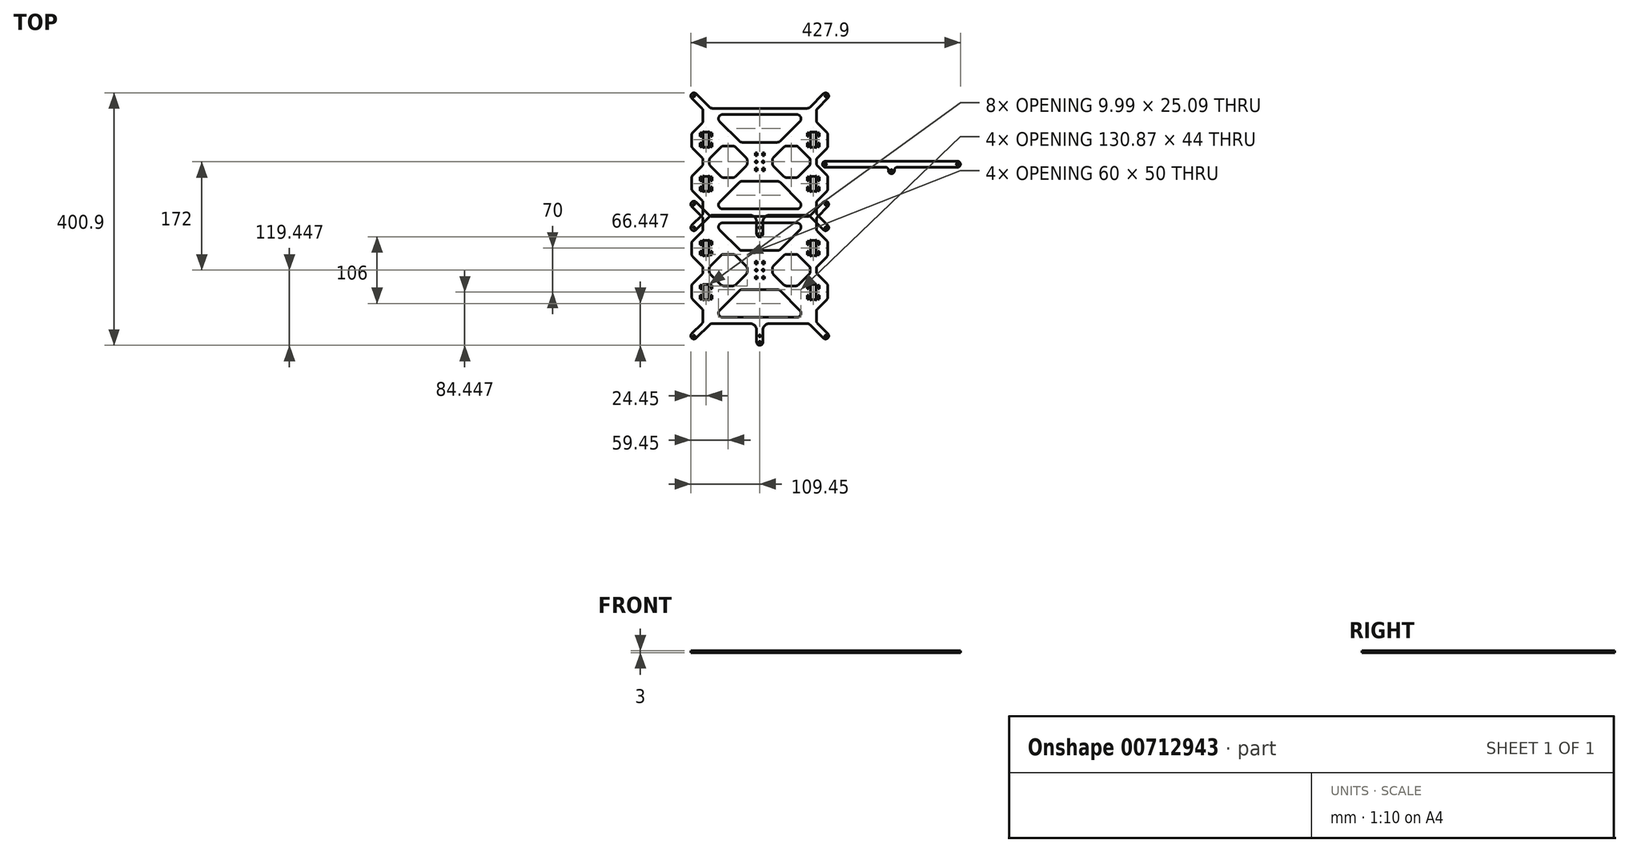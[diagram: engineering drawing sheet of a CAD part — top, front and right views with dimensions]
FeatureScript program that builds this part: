
annotation { "Feature Type Name" : "Feature", "Feature Type Description" : "" }
export const myFeature = defineFeature(function(context is Context, id is Id, definition is map)
    precondition{}
    {
        {
            var Q0;
            Q0=qCreatedBy(makeId("Top.planeOp"),FACE);
            var sketch = newSketch(context, id + "F0", { "sketchPlane" : qUnion([Q0])});
            skCircle(sketch, "E0", {"center": v(5.5, 8.85) * mm, "radius": 1.6 * mm});
            skCircle(sketch, "E1", {"center": v(-104.5, -95.65) * mm, "radius": 1.25 * mm});
            skCircle(sketch, "E2", {"center": v(-104.5, 113.35) * mm, "radius": 1.25 * mm});
            skCircle(sketch, "E3", {"center": v(0, -105.65) * mm, "radius": 1.6 * mm});
            skArc(sketch, "E4", {"start": v(-91.76, 70.09) * mm, "mid": v(-90.46, 72.04) * mm, "end": v(-90, 74.33) * mm});
            skLineSegment(sketch, "E5", {"start": v(-91.76, 70.09) * mm, "end": v(-106.24, 55.6) * mm});
            skArc(sketch, "E6", {"start": v(-106.24, 55.6) * mm, "mid": v(-107.54, 53.66) * mm, "end": v(-108, 51.36) * mm});
            skLineSegment(sketch, "E7", {"start": v(-108, 51.36) * mm, "end": v(-108, 34.33) * mm});
            skArc(sketch, "E8", {"start": v(-108, 34.33) * mm, "mid": v(-107.54, 32.04) * mm, "end": v(-106.24, 30.09) * mm});
            skLineSegment(sketch, "E9", {"start": v(-106.24, 30.09) * mm, "end": v(-91.76, 15.6) * mm});
            skArc(sketch, "E10", {"start": v(-90, 11.36) * mm, "mid": v(-90.46, 13.66) * mm, "end": v(-91.76, 15.6) * mm});
            skLineSegment(sketch, "E11", {"start": v(-90, 11.36) * mm, "end": v(-90, 6.33) * mm});
            skArc(sketch, "E12", {"start": v(-91.76, 2.09) * mm, "mid": v(-90.46, 4.04) * mm, "end": v(-90, 6.33) * mm});
            skLineSegment(sketch, "E13", {"start": v(-91.76, 2.09) * mm, "end": v(-106.24, -12.4) * mm});
            skArc(sketch, "E14", {"start": v(-106.24, -12.4) * mm, "mid": v(-107.54, -14.34) * mm, "end": v(-108, -16.64) * mm});
            skLineSegment(sketch, "E15", {"start": v(-108, -16.64) * mm, "end": v(-108, -33.67) * mm});
            skArc(sketch, "E16", {"start": v(-108, -33.67) * mm, "mid": v(-107.54, -35.96) * mm, "end": v(-106.24, -37.91) * mm});
            skLineSegment(sketch, "E17", {"start": v(-106.24, -37.91) * mm, "end": v(-91.76, -52.4) * mm});
            skArc(sketch, "E18", {"start": v(-90, -56.64) * mm, "mid": v(-90.46, -54.34) * mm, "end": v(-91.76, -52.4) * mm});
            skLineSegment(sketch, "E19", {"start": v(-90, -56.64) * mm, "end": v(-90, -71.67) * mm});
            skArc(sketch, "E20", {"start": v(-91.76, -75.91) * mm, "mid": v(-90.46, -73.96) * mm, "end": v(-90, -71.67) * mm});
            skLineSegment(sketch, "E21", {"start": v(-91.76, -75.91) * mm, "end": v(-108, -92.15) * mm});
            skArc(sketch, "E22", {"start": v(-108, -92.15) * mm, "mid": v(-108, -99.15) * mm, "end": v(-101, -99.15) * mm});
            skLineSegment(sketch, "E23", {"start": v(-101, -99.15) * mm, "end": v(-79.76, -77.91) * mm});
            skArc(sketch, "E24", {"start": v(-75.51, -76.15) * mm, "mid": v(-77.81, -76.6) * mm, "end": v(-79.76, -77.91) * mm});
            skLineSegment(sketch, "E25", {"start": v(-75.51, -76.15) * mm, "end": v(-14.95, -76.15) * mm});
            skArc(sketch, "E26", {"start": v(-4.95, -86.15) * mm, "mid": v(-7.88, -79.08) * mm, "end": v(-14.95, -76.15) * mm});
            skLineSegment(sketch, "E27", {"start": v(-4.95, -86.15) * mm, "end": v(-4.95, -105.65) * mm});
            skArc(sketch, "E28", {"start": v(-4.95, -105.65) * mm, "mid": v(0, -110.6) * mm, "end": v(4.95, -105.65) * mm});
            skLineSegment(sketch, "E29", {"start": v(4.95, -105.65) * mm, "end": v(4.95, -86.15) * mm});
            skArc(sketch, "E30", {"start": v(14.95, -76.15) * mm, "mid": v(7.88, -79.08) * mm, "end": v(4.95, -86.15) * mm});
            skLineSegment(sketch, "E31", {"start": v(14.95, -76.15) * mm, "end": v(75.51, -76.15) * mm});
            skArc(sketch, "E32", {"start": v(79.76, -77.91) * mm, "mid": v(77.81, -76.6) * mm, "end": v(75.51, -76.15) * mm});
            skLineSegment(sketch, "E33", {"start": v(79.76, -77.91) * mm, "end": v(101, -99.15) * mm});
            skArc(sketch, "E34", {"start": v(101, -99.15) * mm, "mid": v(108, -99.15) * mm, "end": v(108, -92.15) * mm});
            skLineSegment(sketch, "E35", {"start": v(108, -92.15) * mm, "end": v(91.76, -75.91) * mm});
            skArc(sketch, "E36", {"start": v(90, -71.67) * mm, "mid": v(90.46, -73.96) * mm, "end": v(91.76, -75.91) * mm});
            skLineSegment(sketch, "E37", {"start": v(90, -71.67) * mm, "end": v(90, -56.64) * mm});
            skArc(sketch, "E38", {"start": v(91.76, -52.4) * mm, "mid": v(90.46, -54.34) * mm, "end": v(90, -56.64) * mm});
            skLineSegment(sketch, "E39", {"start": v(91.76, -52.4) * mm, "end": v(106.24, -37.91) * mm});
            skArc(sketch, "E40", {"start": v(106.24, -37.91) * mm, "mid": v(107.54, -35.96) * mm, "end": v(108, -33.67) * mm});
            skLineSegment(sketch, "E41", {"start": v(108, -33.67) * mm, "end": v(108, -16.64) * mm});
            skArc(sketch, "E42", {"start": v(108, -16.64) * mm, "mid": v(107.54, -14.34) * mm, "end": v(106.24, -12.4) * mm});
            skLineSegment(sketch, "E43", {"start": v(106.24, -12.4) * mm, "end": v(91.76, 2.09) * mm});
            skArc(sketch, "E44", {"start": v(90, 6.33) * mm, "mid": v(90.46, 4.04) * mm, "end": v(91.76, 2.09) * mm});
            skLineSegment(sketch, "E45", {"start": v(90, 6.33) * mm, "end": v(90, 11.36) * mm});
            skArc(sketch, "E46", {"start": v(91.76, 15.6) * mm, "mid": v(90.46, 13.66) * mm, "end": v(90, 11.36) * mm});
            skLineSegment(sketch, "E47", {"start": v(91.76, 15.6) * mm, "end": v(106.24, 30.09) * mm});
            skArc(sketch, "E48", {"start": v(106.24, 30.09) * mm, "mid": v(107.54, 32.04) * mm, "end": v(108, 34.33) * mm});
            skLineSegment(sketch, "E49", {"start": v(108, 34.33) * mm, "end": v(108, 51.36) * mm});
            skArc(sketch, "E50", {"start": v(108, 51.36) * mm, "mid": v(107.54, 53.66) * mm, "end": v(106.24, 55.6) * mm});
            skLineSegment(sketch, "E51", {"start": v(106.24, 55.6) * mm, "end": v(91.76, 70.09) * mm});
            skArc(sketch, "E52", {"start": v(90, 74.33) * mm, "mid": v(90.46, 72.04) * mm, "end": v(91.76, 70.09) * mm});
            skLineSegment(sketch, "E53", {"start": v(90, 74.33) * mm, "end": v(90, 89.36) * mm});
            skArc(sketch, "E54", {"start": v(91.76, 93.6) * mm, "mid": v(90.46, 91.66) * mm, "end": v(90, 89.36) * mm});
            skLineSegment(sketch, "E55", {"start": v(91.76, 93.6) * mm, "end": v(108, 109.85) * mm});
            skArc(sketch, "E56", {"start": v(108, 109.85) * mm, "mid": v(108, 116.85) * mm, "end": v(101, 116.85) * mm});
            skLineSegment(sketch, "E57", {"start": v(101, 116.85) * mm, "end": v(79.76, 95.6) * mm});
            skArc(sketch, "E58", {"start": v(75.51, 93.85) * mm, "mid": v(77.81, 94.3) * mm, "end": v(79.76, 95.6) * mm});
            skLineSegment(sketch, "E59", {"start": v(75.51, 93.85) * mm, "end": v(-75.51, 93.85) * mm});
            skArc(sketch, "E60", {"start": v(-79.76, 95.6) * mm, "mid": v(-77.81, 94.3) * mm, "end": v(-75.51, 93.85) * mm});
            skLineSegment(sketch, "E61", {"start": v(-79.76, 95.6) * mm, "end": v(-101, 116.85) * mm});
            skArc(sketch, "E62", {"start": v(-101, 116.85) * mm, "mid": v(-108, 116.85) * mm, "end": v(-108, 109.85) * mm});
            skLineSegment(sketch, "E63", {"start": v(-108, 109.85) * mm, "end": v(-91.76, 93.6) * mm});
            skArc(sketch, "E64", {"start": v(-90, 89.36) * mm, "mid": v(-90.46, 91.66) * mm, "end": v(-91.76, 93.6) * mm});
            skLineSegment(sketch, "E65", {"start": v(-90, 89.36) * mm, "end": v(-90, 74.33) * mm});
            skLineSegment(sketch, "E66", {"start": v(89.5, -37.34) * mm, "end": v(89.5, -14.97) * mm});
            skArc(sketch, "E67", {"start": v(89.5, -37.34) * mm, "mid": v(89.57, -37.59) * mm, "end": v(89.75, -37.77) * mm});
            skArc(sketch, "E68", {"start": v(89.07, -38.45) * mm, "mid": v(89.85, -38.56) * mm, "end": v(89.75, -37.77) * mm});
            skArc(sketch, "E69", {"start": v(89.07, -38.45) * mm, "mid": v(88.88, -38.27) * mm, "end": v(88.63, -38.2) * mm});
            skLineSegment(sketch, "E70", {"start": v(81.37, -38.2) * mm, "end": v(88.63, -38.2) * mm});
            skArc(sketch, "E71", {"start": v(81.37, -38.2) * mm, "mid": v(81.12, -38.27) * mm, "end": v(80.93, -38.45) * mm});
            skArc(sketch, "E72", {"start": v(80.25, -37.77) * mm, "mid": v(80.15, -38.56) * mm, "end": v(80.93, -38.45) * mm});
            skArc(sketch, "E73", {"start": v(80.25, -37.77) * mm, "mid": v(80.43, -37.59) * mm, "end": v(80.5, -37.34) * mm});
            skLineSegment(sketch, "E74", {"start": v(80.5, -14.97) * mm, "end": v(80.5, -37.34) * mm});
            skArc(sketch, "E75", {"start": v(80.5, -14.97) * mm, "mid": v(80.43, -14.72) * mm, "end": v(80.25, -14.54) * mm});
            skArc(sketch, "E76", {"start": v(80.93, -13.85) * mm, "mid": v(80.15, -13.75) * mm, "end": v(80.25, -14.54) * mm});
            skArc(sketch, "E77", {"start": v(80.93, -13.85) * mm, "mid": v(81.12, -14.04) * mm, "end": v(81.37, -14.1) * mm});
            skLineSegment(sketch, "E78", {"start": v(88.63, -14.1) * mm, "end": v(81.37, -14.1) * mm});
            skArc(sketch, "E79", {"start": v(88.63, -14.1) * mm, "mid": v(88.88, -14.04) * mm, "end": v(89.07, -13.85) * mm});
            skArc(sketch, "E80", {"start": v(89.75, -14.54) * mm, "mid": v(89.85, -13.75) * mm, "end": v(89.07, -13.85) * mm});
            skArc(sketch, "E81", {"start": v(89.75, -14.54) * mm, "mid": v(89.57, -14.72) * mm, "end": v(89.5, -14.97) * mm});
            skLineSegment(sketch, "E82", {"start": v(32.73, 41.78) * mm, "end": v(63.53, 72.58) * mm});
            skArc(sketch, "E83", {"start": v(28.07, 39.85) * mm, "mid": v(30.6, 40.35) * mm, "end": v(32.73, 41.78) * mm});
            skLineSegment(sketch, "E84", {"start": v(-28.07, 39.85) * mm, "end": v(28.07, 39.85) * mm});
            skArc(sketch, "E85", {"start": v(-32.73, 41.78) * mm, "mid": v(-30.6, 40.35) * mm, "end": v(-28.07, 39.85) * mm});
            skLineSegment(sketch, "E86", {"start": v(-63.53, 72.58) * mm, "end": v(-32.73, 41.78) * mm});
            skArc(sketch, "E87", {"start": v(-58.87, 83.85) * mm, "mid": v(-64.96, 79.77) * mm, "end": v(-63.53, 72.58) * mm});
            skLineSegment(sketch, "E88", {"start": v(58.87, 83.85) * mm, "end": v(-58.87, 83.85) * mm});
            skArc(sketch, "E89", {"start": v(63.53, 72.58) * mm, "mid": v(64.96, 79.77) * mm, "end": v(58.87, 83.85) * mm});
            skLineSegment(sketch, "E90", {"start": v(21.76, 2.09) * mm, "end": v(38.24, -14.4) * mm});
            skArc(sketch, "E91", {"start": v(20, 6.33) * mm, "mid": v(20.46, 4.04) * mm, "end": v(21.76, 2.09) * mm});
            skLineSegment(sketch, "E92", {"start": v(20, 11.36) * mm, "end": v(20, 6.33) * mm});
            skArc(sketch, "E93", {"start": v(21.76, 15.6) * mm, "mid": v(20.46, 13.66) * mm, "end": v(20, 11.36) * mm});
            skLineSegment(sketch, "E94", {"start": v(38.24, 32.09) * mm, "end": v(21.76, 15.6) * mm});
            skArc(sketch, "E95", {"start": v(42.49, 33.85) * mm, "mid": v(40.19, 33.4) * mm, "end": v(38.24, 32.09) * mm});
            skLineSegment(sketch, "E96", {"start": v(57.51, 33.85) * mm, "end": v(42.49, 33.85) * mm});
            skArc(sketch, "E97", {"start": v(61.76, 32.09) * mm, "mid": v(59.81, 33.4) * mm, "end": v(57.51, 33.85) * mm});
            skLineSegment(sketch, "E98", {"start": v(78.24, 15.6) * mm, "end": v(61.76, 32.09) * mm});
            skArc(sketch, "E99", {"start": v(80, 11.36) * mm, "mid": v(79.54, 13.66) * mm, "end": v(78.24, 15.6) * mm});
            skLineSegment(sketch, "E100", {"start": v(80, 6.33) * mm, "end": v(80, 11.36) * mm});
            skArc(sketch, "E101", {"start": v(78.24, 2.09) * mm, "mid": v(79.54, 4.04) * mm, "end": v(80, 6.33) * mm});
            skLineSegment(sketch, "E102", {"start": v(61.76, -14.4) * mm, "end": v(78.24, 2.09) * mm});
            skArc(sketch, "E103", {"start": v(57.51, -16.15) * mm, "mid": v(59.81, -15.7) * mm, "end": v(61.76, -14.4) * mm});
            skLineSegment(sketch, "E104", {"start": v(42.49, -16.15) * mm, "end": v(57.51, -16.15) * mm});
            skArc(sketch, "E105", {"start": v(38.24, -14.4) * mm, "mid": v(40.19, -15.7) * mm, "end": v(42.49, -16.15) * mm});
            skLineSegment(sketch, "E106", {"start": v(63.53, -54.89) * mm, "end": v(32.73, -24.09) * mm});
            skArc(sketch, "E107", {"start": v(58.87, -66.15) * mm, "mid": v(64.96, -62.08) * mm, "end": v(63.53, -54.89) * mm});
            skLineSegment(sketch, "E108", {"start": v(-58.87, -66.15) * mm, "end": v(58.87, -66.15) * mm});
            skArc(sketch, "E109", {"start": v(-63.53, -54.89) * mm, "mid": v(-64.96, -62.08) * mm, "end": v(-58.87, -66.15) * mm});
            skLineSegment(sketch, "E110", {"start": v(-32.73, -24.09) * mm, "end": v(-63.53, -54.89) * mm});
            skArc(sketch, "E111", {"start": v(-28.07, -22.15) * mm, "mid": v(-30.6, -22.66) * mm, "end": v(-32.73, -24.09) * mm});
            skLineSegment(sketch, "E112", {"start": v(28.07, -22.15) * mm, "end": v(-28.07, -22.15) * mm});
            skArc(sketch, "E113", {"start": v(32.73, -24.09) * mm, "mid": v(30.6, -22.66) * mm, "end": v(28.07, -22.15) * mm});
            skLineSegment(sketch, "E114", {"start": v(-61.76, 32.09) * mm, "end": v(-78.24, 15.6) * mm});
            skArc(sketch, "E115", {"start": v(-57.51, 33.85) * mm, "mid": v(-59.81, 33.4) * mm, "end": v(-61.76, 32.09) * mm});
            skLineSegment(sketch, "E116", {"start": v(-42.49, 33.85) * mm, "end": v(-57.51, 33.85) * mm});
            skArc(sketch, "E117", {"start": v(-38.24, 32.09) * mm, "mid": v(-40.19, 33.4) * mm, "end": v(-42.49, 33.85) * mm});
            skLineSegment(sketch, "E118", {"start": v(-21.76, 15.6) * mm, "end": v(-38.24, 32.09) * mm});
            skArc(sketch, "E119", {"start": v(-20, 11.36) * mm, "mid": v(-20.46, 13.66) * mm, "end": v(-21.76, 15.6) * mm});
            skLineSegment(sketch, "E120", {"start": v(-20, 6.33) * mm, "end": v(-20, 11.36) * mm});
            skArc(sketch, "E121", {"start": v(-21.76, 2.09) * mm, "mid": v(-20.46, 4.04) * mm, "end": v(-20, 6.33) * mm});
            skLineSegment(sketch, "E122", {"start": v(-38.24, -14.4) * mm, "end": v(-21.76, 2.09) * mm});
            skArc(sketch, "E123", {"start": v(-42.49, -16.15) * mm, "mid": v(-40.19, -15.7) * mm, "end": v(-38.24, -14.4) * mm});
            skLineSegment(sketch, "E124", {"start": v(-57.51, -16.15) * mm, "end": v(-42.49, -16.15) * mm});
            skArc(sketch, "E125", {"start": v(-61.76, -14.4) * mm, "mid": v(-59.81, -15.7) * mm, "end": v(-57.51, -16.15) * mm});
            skLineSegment(sketch, "E126", {"start": v(-78.24, 2.09) * mm, "end": v(-61.76, -14.4) * mm});
            skArc(sketch, "E127", {"start": v(-80, 6.33) * mm, "mid": v(-79.54, 4.04) * mm, "end": v(-78.24, 2.09) * mm});
            skLineSegment(sketch, "E128", {"start": v(-80, 11.36) * mm, "end": v(-80, 6.33) * mm});
            skArc(sketch, "E129", {"start": v(-78.24, 15.6) * mm, "mid": v(-79.54, 13.66) * mm, "end": v(-80, 11.36) * mm});
            skLineSegment(sketch, "E130", {"start": v(-88.63, 31.8) * mm, "end": v(-81.37, 31.8) * mm});
            skArc(sketch, "E131", {"start": v(-88.63, 31.8) * mm, "mid": v(-88.88, 31.73) * mm, "end": v(-89.07, 31.55) * mm});
            skArc(sketch, "E132", {"start": v(-89.75, 32.23) * mm, "mid": v(-89.85, 31.44) * mm, "end": v(-89.07, 31.55) * mm});
            skArc(sketch, "E133", {"start": v(-89.75, 32.23) * mm, "mid": v(-89.57, 32.41) * mm, "end": v(-89.5, 32.66) * mm});
            skLineSegment(sketch, "E134", {"start": v(-89.5, 55.03) * mm, "end": v(-89.5, 32.66) * mm});
            skArc(sketch, "E135", {"start": v(-89.5, 55.03) * mm, "mid": v(-89.57, 55.28) * mm, "end": v(-89.75, 55.46) * mm});
            skArc(sketch, "E136", {"start": v(-89.07, 56.15) * mm, "mid": v(-89.85, 56.25) * mm, "end": v(-89.75, 55.46) * mm});
            skArc(sketch, "E137", {"start": v(-89.07, 56.15) * mm, "mid": v(-88.88, 55.96) * mm, "end": v(-88.63, 55.9) * mm});
            skLineSegment(sketch, "E138", {"start": v(-81.37, 55.9) * mm, "end": v(-88.63, 55.9) * mm});
            skArc(sketch, "E139", {"start": v(-81.37, 55.9) * mm, "mid": v(-81.12, 55.96) * mm, "end": v(-80.93, 56.15) * mm});
            skArc(sketch, "E140", {"start": v(-80.25, 55.46) * mm, "mid": v(-80.15, 56.25) * mm, "end": v(-80.93, 56.15) * mm});
            skArc(sketch, "E141", {"start": v(-80.25, 55.46) * mm, "mid": v(-80.43, 55.28) * mm, "end": v(-80.5, 55.03) * mm});
            skLineSegment(sketch, "E142", {"start": v(-80.5, 32.66) * mm, "end": v(-80.5, 55.03) * mm});
            skArc(sketch, "E143", {"start": v(-80.5, 32.66) * mm, "mid": v(-80.43, 32.41) * mm, "end": v(-80.25, 32.23) * mm});
            skArc(sketch, "E144", {"start": v(-80.93, 31.55) * mm, "mid": v(-80.15, 31.44) * mm, "end": v(-80.25, 32.23) * mm});
            skArc(sketch, "E145", {"start": v(-80.93, 31.55) * mm, "mid": v(-81.12, 31.73) * mm, "end": v(-81.37, 31.8) * mm});
            skLineSegment(sketch, "E146", {"start": v(-88.63, -38.2) * mm, "end": v(-81.37, -38.2) * mm});
            skArc(sketch, "E147", {"start": v(-88.63, -38.2) * mm, "mid": v(-88.88, -38.27) * mm, "end": v(-89.07, -38.45) * mm});
            skArc(sketch, "E148", {"start": v(-89.75, -37.77) * mm, "mid": v(-89.85, -38.56) * mm, "end": v(-89.07, -38.45) * mm});
            skArc(sketch, "E149", {"start": v(-89.75, -37.77) * mm, "mid": v(-89.57, -37.59) * mm, "end": v(-89.5, -37.34) * mm});
            skLineSegment(sketch, "E150", {"start": v(-89.5, -14.97) * mm, "end": v(-89.5, -37.34) * mm});
            skArc(sketch, "E151", {"start": v(-89.5, -14.97) * mm, "mid": v(-89.57, -14.72) * mm, "end": v(-89.75, -14.54) * mm});
            skArc(sketch, "E152", {"start": v(-89.07, -13.85) * mm, "mid": v(-89.85, -13.75) * mm, "end": v(-89.75, -14.54) * mm});
            skArc(sketch, "E153", {"start": v(-89.07, -13.85) * mm, "mid": v(-88.88, -14.04) * mm, "end": v(-88.63, -14.1) * mm});
            skLineSegment(sketch, "E154", {"start": v(-81.37, -14.1) * mm, "end": v(-88.63, -14.1) * mm});
            skArc(sketch, "E155", {"start": v(-81.37, -14.1) * mm, "mid": v(-81.12, -14.04) * mm, "end": v(-80.93, -13.85) * mm});
            skArc(sketch, "E156", {"start": v(-80.25, -14.54) * mm, "mid": v(-80.15, -13.75) * mm, "end": v(-80.93, -13.85) * mm});
            skArc(sketch, "E157", {"start": v(-80.25, -14.54) * mm, "mid": v(-80.43, -14.72) * mm, "end": v(-80.5, -14.97) * mm});
            skLineSegment(sketch, "E158", {"start": v(-80.5, -37.34) * mm, "end": v(-80.5, -14.97) * mm});
            skArc(sketch, "E159", {"start": v(-80.5, -37.34) * mm, "mid": v(-80.43, -37.59) * mm, "end": v(-80.25, -37.77) * mm});
            skArc(sketch, "E160", {"start": v(-80.93, -38.45) * mm, "mid": v(-80.15, -38.56) * mm, "end": v(-80.25, -37.77) * mm});
            skArc(sketch, "E161", {"start": v(-80.93, -38.45) * mm, "mid": v(-81.12, -38.27) * mm, "end": v(-81.37, -38.2) * mm});
            skLineSegment(sketch, "E162", {"start": v(89.5, 32.66) * mm, "end": v(89.5, 55.03) * mm});
            skArc(sketch, "E163", {"start": v(89.5, 32.66) * mm, "mid": v(89.57, 32.41) * mm, "end": v(89.75, 32.23) * mm});
            skArc(sketch, "E164", {"start": v(89.07, 31.55) * mm, "mid": v(89.85, 31.44) * mm, "end": v(89.75, 32.23) * mm});
            skArc(sketch, "E165", {"start": v(89.07, 31.55) * mm, "mid": v(88.88, 31.73) * mm, "end": v(88.63, 31.8) * mm});
            skLineSegment(sketch, "E166", {"start": v(81.37, 31.8) * mm, "end": v(88.63, 31.8) * mm});
            skArc(sketch, "E167", {"start": v(81.37, 31.8) * mm, "mid": v(81.12, 31.73) * mm, "end": v(80.93, 31.55) * mm});
            skArc(sketch, "E168", {"start": v(80.25, 32.23) * mm, "mid": v(80.15, 31.44) * mm, "end": v(80.93, 31.55) * mm});
            skArc(sketch, "E169", {"start": v(80.25, 32.23) * mm, "mid": v(80.43, 32.41) * mm, "end": v(80.5, 32.66) * mm});
            skLineSegment(sketch, "E170", {"start": v(80.5, 55.03) * mm, "end": v(80.5, 32.66) * mm});
            skArc(sketch, "E171", {"start": v(80.5, 55.03) * mm, "mid": v(80.43, 55.28) * mm, "end": v(80.25, 55.46) * mm});
            skArc(sketch, "E172", {"start": v(80.93, 56.15) * mm, "mid": v(80.15, 56.25) * mm, "end": v(80.25, 55.46) * mm});
            skArc(sketch, "E173", {"start": v(80.93, 56.15) * mm, "mid": v(81.12, 55.96) * mm, "end": v(81.37, 55.9) * mm});
            skLineSegment(sketch, "E174", {"start": v(88.63, 55.9) * mm, "end": v(81.37, 55.9) * mm});
            skArc(sketch, "E175", {"start": v(88.63, 55.9) * mm, "mid": v(88.88, 55.96) * mm, "end": v(89.07, 56.15) * mm});
            skArc(sketch, "E176", {"start": v(89.75, 55.46) * mm, "mid": v(89.85, 56.25) * mm, "end": v(89.07, 56.15) * mm});
            skArc(sketch, "E177", {"start": v(89.75, 55.46) * mm, "mid": v(89.57, 55.28) * mm, "end": v(89.5, 55.03) * mm});
            skCircle(sketch, "E178", {"center": v(0, -95.65) * mm, "radius": 1.6 * mm});
            skCircle(sketch, "E179", {"center": v(104.5, 113.35) * mm, "radius": 1.25 * mm});
            skCircle(sketch, "E180", {"center": v(104.5, -95.65) * mm, "radius": 1.25 * mm});
            skCircle(sketch, "E181", {"center": v(-5.5, 8.85) * mm, "radius": 1.6 * mm});
            skLineSegment(sketch, "E182", {"start": v(7.2, -1.05) * mm, "end": v(4, -1.05) * mm});
            skLineSegment(sketch, "E183", {"start": v(7.2, -5.25) * mm, "end": v(7.2, -1.05) * mm});
            skLineSegment(sketch, "E184", {"start": v(4, -5.25) * mm, "end": v(7.2, -5.25) * mm});
            skLineSegment(sketch, "E185", {"start": v(4, -1.05) * mm, "end": v(4, -5.25) * mm});
            skLineSegment(sketch, "E186", {"start": v(7.2, 22.95) * mm, "end": v(4, 22.95) * mm});
            skLineSegment(sketch, "E187", {"start": v(7.2, 18.75) * mm, "end": v(7.2, 22.95) * mm});
            skLineSegment(sketch, "E188", {"start": v(4, 18.75) * mm, "end": v(7.2, 18.75) * mm});
            skLineSegment(sketch, "E189", {"start": v(4, 22.95) * mm, "end": v(4, 18.75) * mm});
            skLineSegment(sketch, "E190", {"start": v(-7.2, -5.25) * mm, "end": v(-4, -5.25) * mm});
            skLineSegment(sketch, "E191", {"start": v(-7.2, -1.05) * mm, "end": v(-7.2, -5.25) * mm});
            skLineSegment(sketch, "E192", {"start": v(-4, -1.05) * mm, "end": v(-7.2, -1.05) * mm});
            skLineSegment(sketch, "E193", {"start": v(-4, -5.25) * mm, "end": v(-4, -1.05) * mm});
            skLineSegment(sketch, "E194", {"start": v(-7.2, 18.75) * mm, "end": v(-4, 18.75) * mm});
            skLineSegment(sketch, "E195", {"start": v(-7.2, 22.95) * mm, "end": v(-7.2, 18.75) * mm});
            skLineSegment(sketch, "E196", {"start": v(-4, 22.95) * mm, "end": v(-7.2, 22.95) * mm});
            skLineSegment(sketch, "E197", {"start": v(-4, 18.75) * mm, "end": v(-4, 22.95) * mm});
            skLineSegment(sketch, "E198", {"start": v(-75.5, 38.85) * mm, "end": v(-77.5, 38.85) * mm});
            skLineSegment(sketch, "E199", {"start": v(-75.5, 32.85) * mm, "end": v(-75.5, 38.85) * mm});
            skLineSegment(sketch, "E200", {"start": v(-77.5, 32.85) * mm, "end": v(-75.5, 32.85) * mm});
            skLineSegment(sketch, "E201", {"start": v(-77.5, 38.85) * mm, "end": v(-77.5, 32.85) * mm});
            skLineSegment(sketch, "E202", {"start": v(-92.5, 38.85) * mm, "end": v(-94.5, 38.85) * mm});
            skLineSegment(sketch, "E203", {"start": v(-92.5, 32.85) * mm, "end": v(-92.5, 38.85) * mm});
            skLineSegment(sketch, "E204", {"start": v(-94.5, 32.85) * mm, "end": v(-92.5, 32.85) * mm});
            skLineSegment(sketch, "E205", {"start": v(-94.5, 38.85) * mm, "end": v(-94.5, 32.85) * mm});
            skLineSegment(sketch, "E206", {"start": v(-77.5, 48.85) * mm, "end": v(-75.5, 48.85) * mm});
            skLineSegment(sketch, "E207", {"start": v(-77.5, 54.85) * mm, "end": v(-77.5, 48.85) * mm});
            skLineSegment(sketch, "E208", {"start": v(-75.5, 54.85) * mm, "end": v(-77.5, 54.85) * mm});
            skLineSegment(sketch, "E209", {"start": v(-75.5, 48.85) * mm, "end": v(-75.5, 54.85) * mm});
            skLineSegment(sketch, "E210", {"start": v(-94.5, 48.85) * mm, "end": v(-92.5, 48.85) * mm});
            skLineSegment(sketch, "E211", {"start": v(-94.5, 54.85) * mm, "end": v(-94.5, 48.85) * mm});
            skLineSegment(sketch, "E212", {"start": v(-92.5, 54.85) * mm, "end": v(-94.5, 54.85) * mm});
            skLineSegment(sketch, "E213", {"start": v(-92.5, 48.85) * mm, "end": v(-92.5, 54.85) * mm});
            skLineSegment(sketch, "E214", {"start": v(94.5, 38.85) * mm, "end": v(92.5, 38.85) * mm});
            skLineSegment(sketch, "E215", {"start": v(94.5, 32.85) * mm, "end": v(94.5, 38.85) * mm});
            skLineSegment(sketch, "E216", {"start": v(92.5, 32.85) * mm, "end": v(94.5, 32.85) * mm});
            skLineSegment(sketch, "E217", {"start": v(92.5, 38.85) * mm, "end": v(92.5, 32.85) * mm});
            skLineSegment(sketch, "E218", {"start": v(77.5, 38.85) * mm, "end": v(75.5, 38.85) * mm});
            skLineSegment(sketch, "E219", {"start": v(77.5, 32.85) * mm, "end": v(77.5, 38.85) * mm});
            skLineSegment(sketch, "E220", {"start": v(75.5, 32.85) * mm, "end": v(77.5, 32.85) * mm});
            skLineSegment(sketch, "E221", {"start": v(75.5, 38.85) * mm, "end": v(75.5, 32.85) * mm});
            skLineSegment(sketch, "E222", {"start": v(92.5, 48.85) * mm, "end": v(94.5, 48.85) * mm});
            skLineSegment(sketch, "E223", {"start": v(92.5, 54.85) * mm, "end": v(92.5, 48.85) * mm});
            skLineSegment(sketch, "E224", {"start": v(94.5, 54.85) * mm, "end": v(92.5, 54.85) * mm});
            skLineSegment(sketch, "E225", {"start": v(94.5, 48.85) * mm, "end": v(94.5, 54.85) * mm});
            skLineSegment(sketch, "E226", {"start": v(75.5, 48.85) * mm, "end": v(77.5, 48.85) * mm});
            skLineSegment(sketch, "E227", {"start": v(75.5, 54.85) * mm, "end": v(75.5, 48.85) * mm});
            skLineSegment(sketch, "E228", {"start": v(77.5, 54.85) * mm, "end": v(75.5, 54.85) * mm});
            skLineSegment(sketch, "E229", {"start": v(77.5, 48.85) * mm, "end": v(77.5, 54.85) * mm});
            skLineSegment(sketch, "E230", {"start": v(94.5, -31.15) * mm, "end": v(92.5, -31.15) * mm});
            skLineSegment(sketch, "E231", {"start": v(94.5, -37.15) * mm, "end": v(94.5, -31.15) * mm});
            skLineSegment(sketch, "E232", {"start": v(92.5, -37.15) * mm, "end": v(94.5, -37.15) * mm});
            skLineSegment(sketch, "E233", {"start": v(92.5, -31.15) * mm, "end": v(92.5, -37.15) * mm});
            skLineSegment(sketch, "E234", {"start": v(77.5, -31.15) * mm, "end": v(75.5, -31.15) * mm});
            skLineSegment(sketch, "E235", {"start": v(77.5, -37.15) * mm, "end": v(77.5, -31.15) * mm});
            skLineSegment(sketch, "E236", {"start": v(75.5, -37.15) * mm, "end": v(77.5, -37.15) * mm});
            skLineSegment(sketch, "E237", {"start": v(75.5, -31.15) * mm, "end": v(75.5, -37.15) * mm});
            skLineSegment(sketch, "E238", {"start": v(92.5, -21.15) * mm, "end": v(94.5, -21.15) * mm});
            skLineSegment(sketch, "E239", {"start": v(92.5, -15.15) * mm, "end": v(92.5, -21.15) * mm});
            skLineSegment(sketch, "E240", {"start": v(94.5, -15.15) * mm, "end": v(92.5, -15.15) * mm});
            skLineSegment(sketch, "E241", {"start": v(94.5, -21.15) * mm, "end": v(94.5, -15.15) * mm});
            skLineSegment(sketch, "E242", {"start": v(75.5, -21.15) * mm, "end": v(77.5, -21.15) * mm});
            skLineSegment(sketch, "E243", {"start": v(75.5, -15.15) * mm, "end": v(75.5, -21.15) * mm});
            skLineSegment(sketch, "E244", {"start": v(77.5, -15.15) * mm, "end": v(75.5, -15.15) * mm});
            skLineSegment(sketch, "E245", {"start": v(77.5, -21.15) * mm, "end": v(77.5, -15.15) * mm});
            skLineSegment(sketch, "E246", {"start": v(-75.5, -31.15) * mm, "end": v(-77.5, -31.15) * mm});
            skLineSegment(sketch, "E247", {"start": v(-75.5, -37.15) * mm, "end": v(-75.5, -31.15) * mm});
            skLineSegment(sketch, "E248", {"start": v(-77.5, -37.15) * mm, "end": v(-75.5, -37.15) * mm});
            skLineSegment(sketch, "E249", {"start": v(-77.5, -31.15) * mm, "end": v(-77.5, -37.15) * mm});
            skLineSegment(sketch, "E250", {"start": v(-92.5, -31.15) * mm, "end": v(-94.5, -31.15) * mm});
            skLineSegment(sketch, "E251", {"start": v(-92.5, -37.15) * mm, "end": v(-92.5, -31.15) * mm});
            skLineSegment(sketch, "E252", {"start": v(-94.5, -37.15) * mm, "end": v(-92.5, -37.15) * mm});
            skLineSegment(sketch, "E253", {"start": v(-94.5, -31.15) * mm, "end": v(-94.5, -37.15) * mm});
            skLineSegment(sketch, "E254", {"start": v(-77.5, -21.15) * mm, "end": v(-75.5, -21.15) * mm});
            skLineSegment(sketch, "E255", {"start": v(-77.5, -15.15) * mm, "end": v(-77.5, -21.15) * mm});
            skLineSegment(sketch, "E256", {"start": v(-75.5, -15.15) * mm, "end": v(-77.5, -15.15) * mm});
            skLineSegment(sketch, "E257", {"start": v(-75.5, -21.15) * mm, "end": v(-75.5, -15.15) * mm});
            skLineSegment(sketch, "E258", {"start": v(-94.5, -21.15) * mm, "end": v(-92.5, -21.15) * mm});
            skLineSegment(sketch, "E259", {"start": v(-94.5, -15.15) * mm, "end": v(-94.5, -21.15) * mm});
            skLineSegment(sketch, "E260", {"start": v(-92.5, -15.15) * mm, "end": v(-94.5, -15.15) * mm});
            skLineSegment(sketch, "E261", {"start": v(-92.5, -21.15) * mm, "end": v(-92.5, -15.15) * mm});
            skSolve(sketch);
        }
        {
            var Q0;
            Q0 = qSketchRegion(id + "F0", true);
            extrude(context, id + "F1", {"entities" : qUnion([Q0]), "depth" : 3 * mm, "offsetDistance" : 25 * mm});
        }
        {
            var Q0;
            Q0=qCreatedBy(makeId("Top.planeOp"),FACE);
            var sketch = newSketch(context, id + "F2", { "sketchPlane" : qUnion([Q0])});
            skArc(sketch, "E262", {"start": v(104.5, 0.05) * mm, "mid": v(109.45, 5) * mm, "end": v(104.5, 9.95) * mm});
            skArc(sketch, "E263", {"start": v(-104.5, 9.95) * mm, "mid": v(-109.45, 5) * mm, "end": v(-104.5, 0.05) * mm});
            skCircle(sketch, "E264", {"center": v(-104.5, 5) * mm, "radius": 1.6 * mm});
            skCircle(sketch, "E265", {"center": v(104.5, 5) * mm, "radius": 1.6 * mm});
            skArc(sketch, "E266", {"start": v(-4.95, -5) * mm, "mid": v(0, -9.95) * mm, "end": v(4.95, -5) * mm});
            skCircle(sketch, "E267", {"center": v(0, -5) * mm, "radius": 1.6 * mm});
            skLineSegment(sketch, "E268", {"start": v(-8.95, 0.05) * mm, "end": v(-104.5, 0.05) * mm});
            skLineSegment(sketch, "E269", {"start": v(-4.95, -5) * mm, "end": v(-4.95, -3.95) * mm});
            skLineSegment(sketch, "E270", {"start": v(4.95, -3.95) * mm, "end": v(4.95, -5) * mm});
            skLineSegment(sketch, "E271", {"start": v(104.5, 0.05) * mm, "end": v(8.95, 0.05) * mm});
            skLineSegment(sketch, "E272", {"start": v(-104.5, 9.95) * mm, "end": v(104.5, 9.95) * mm});
            skArc(sketch, "E273", {"start": v(8.95, 0.05) * mm, "mid": v(6.12, -1.12) * mm, "end": v(4.95, -3.95) * mm});
            skArc(sketch, "E274", {"start": v(-4.95, -3.95) * mm, "mid": v(-6.12, -1.12) * mm, "end": v(-8.95, 0.05) * mm});
            skSolve(sketch);
        }
        {
            var Q0;
            Q0 = qSketchRegion(id + "F2", true);
            extrude(context, id + "F3", {"entities" : qUnion([Q0]), "depth" : 3 * mm, "offsetDistance" : 25 * mm});
        }
        {
            var Q0;
            Q0=makeQuery(id+"F3.opExtrude","SWEPT_BODY",BODY,{"disambiguationData":[OSD([sQuery(id+"F2.wireOp",EDGE,"E262"),sQuery(id+"F2.wireOp",EDGE,"E263"),sQuery(id+"F2.wireOp",EDGE,"E264"),sQuery(id+"F2.wireOp",EDGE,"E265"),sQuery(id+"F2.wireOp",EDGE,"E266"),sQuery(id+"F2.wireOp",EDGE,"E267"),sQuery(id+"F2.wireOp",EDGE,"E268"),sQuery(id+"F2.wireOp",EDGE,"E269"),sQuery(id+"F2.wireOp",EDGE,"E270"),sQuery(id+"F2.wireOp",EDGE,"E271"),sQuery(id+"F2.wireOp",EDGE,"E272"),sQuery(id+"F2.wireOp",EDGE,"E273"),sQuery(id+"F2.wireOp",EDGE,"E274")])]});
            var Q1;
            Q1=makeQuery(id+"F3.opExtrude","CAP_EDGE",EDGE,{"disambiguationData":[OSD([sQuery(id+"F2.wireOp",EDGE,"E272")])],"isStart":false});
            transform(context, id + "F4", {"entities" : qUnion([Q0]), "transformType" : TransformType.TRANSLATION_ENTITY, "oppositeDirectionEntity" : false, "transformLine" : qUnion([Q1]), "makeCopy" : false});
        }
        {
            var Q0;
            Q0=makeQuery(id+"F1.opExtrude","SWEPT_BODY",BODY,{"disambiguationData":[OSD([sQuery(id+"F0.wireOp",EDGE,"E0"),sQuery(id+"F0.wireOp",EDGE,"E1"),sQuery(id+"F0.wireOp",EDGE,"E2"),sQuery(id+"F0.wireOp",EDGE,"E3"),sQuery(id+"F0.wireOp",EDGE,"E4"),sQuery(id+"F0.wireOp",EDGE,"E5"),sQuery(id+"F0.wireOp",EDGE,"E6"),sQuery(id+"F0.wireOp",EDGE,"E7"),sQuery(id+"F0.wireOp",EDGE,"E8"),sQuery(id+"F0.wireOp",EDGE,"E9"),sQuery(id+"F0.wireOp",EDGE,"E10"),sQuery(id+"F0.wireOp",EDGE,"E11"),sQuery(id+"F0.wireOp",EDGE,"E12"),sQuery(id+"F0.wireOp",EDGE,"E13"),sQuery(id+"F0.wireOp",EDGE,"E14"),sQuery(id+"F0.wireOp",EDGE,"E15"),sQuery(id+"F0.wireOp",EDGE,"E16"),sQuery(id+"F0.wireOp",EDGE,"E17"),sQuery(id+"F0.wireOp",EDGE,"E18"),sQuery(id+"F0.wireOp",EDGE,"E19"),sQuery(id+"F0.wireOp",EDGE,"E20"),sQuery(id+"F0.wireOp",EDGE,"E21"),sQuery(id+"F0.wireOp",EDGE,"E22"),sQuery(id+"F0.wireOp",EDGE,"E23"),sQuery(id+"F0.wireOp",EDGE,"E24"),sQuery(id+"F0.wireOp",EDGE,"E25"),sQuery(id+"F0.wireOp",EDGE,"E26"),sQuery(id+"F0.wireOp",EDGE,"E27"),sQuery(id+"F0.wireOp",EDGE,"E28"),sQuery(id+"F0.wireOp",EDGE,"E29"),sQuery(id+"F0.wireOp",EDGE,"E30"),sQuery(id+"F0.wireOp",EDGE,"E31"),sQuery(id+"F0.wireOp",EDGE,"E32"),sQuery(id+"F0.wireOp",EDGE,"E33"),sQuery(id+"F0.wireOp",EDGE,"E34"),sQuery(id+"F0.wireOp",EDGE,"E35"),sQuery(id+"F0.wireOp",EDGE,"E36"),sQuery(id+"F0.wireOp",EDGE,"E37"),sQuery(id+"F0.wireOp",EDGE,"E38"),sQuery(id+"F0.wireOp",EDGE,"E39"),sQuery(id+"F0.wireOp",EDGE,"E40"),sQuery(id+"F0.wireOp",EDGE,"E41"),sQuery(id+"F0.wireOp",EDGE,"E42"),sQuery(id+"F0.wireOp",EDGE,"E43"),sQuery(id+"F0.wireOp",EDGE,"E44"),sQuery(id+"F0.wireOp",EDGE,"E45"),sQuery(id+"F0.wireOp",EDGE,"E46"),sQuery(id+"F0.wireOp",EDGE,"E47"),sQuery(id+"F0.wireOp",EDGE,"E48"),sQuery(id+"F0.wireOp",EDGE,"E49"),sQuery(id+"F0.wireOp",EDGE,"E50"),sQuery(id+"F0.wireOp",EDGE,"E51"),sQuery(id+"F0.wireOp",EDGE,"E52"),sQuery(id+"F0.wireOp",EDGE,"E53"),sQuery(id+"F0.wireOp",EDGE,"E54"),sQuery(id+"F0.wireOp",EDGE,"E55"),sQuery(id+"F0.wireOp",EDGE,"E56"),sQuery(id+"F0.wireOp",EDGE,"E57"),sQuery(id+"F0.wireOp",EDGE,"E58"),sQuery(id+"F0.wireOp",EDGE,"E59"),sQuery(id+"F0.wireOp",EDGE,"E60"),sQuery(id+"F0.wireOp",EDGE,"E61"),sQuery(id+"F0.wireOp",EDGE,"E62"),sQuery(id+"F0.wireOp",EDGE,"E63"),sQuery(id+"F0.wireOp",EDGE,"E64"),sQuery(id+"F0.wireOp",EDGE,"E65"),sQuery(id+"F0.wireOp",EDGE,"E66"),sQuery(id+"F0.wireOp",EDGE,"E67"),sQuery(id+"F0.wireOp",EDGE,"E68"),sQuery(id+"F0.wireOp",EDGE,"E69"),sQuery(id+"F0.wireOp",EDGE,"E70"),sQuery(id+"F0.wireOp",EDGE,"E71"),sQuery(id+"F0.wireOp",EDGE,"E72"),sQuery(id+"F0.wireOp",EDGE,"E73"),sQuery(id+"F0.wireOp",EDGE,"E74"),sQuery(id+"F0.wireOp",EDGE,"E75"),sQuery(id+"F0.wireOp",EDGE,"E76"),sQuery(id+"F0.wireOp",EDGE,"E77"),sQuery(id+"F0.wireOp",EDGE,"E78"),sQuery(id+"F0.wireOp",EDGE,"E79"),sQuery(id+"F0.wireOp",EDGE,"E80"),sQuery(id+"F0.wireOp",EDGE,"E81"),sQuery(id+"F0.wireOp",EDGE,"E82"),sQuery(id+"F0.wireOp",EDGE,"E83"),sQuery(id+"F0.wireOp",EDGE,"E84"),sQuery(id+"F0.wireOp",EDGE,"E85"),sQuery(id+"F0.wireOp",EDGE,"E86"),sQuery(id+"F0.wireOp",EDGE,"E87"),sQuery(id+"F0.wireOp",EDGE,"E88"),sQuery(id+"F0.wireOp",EDGE,"E89"),sQuery(id+"F0.wireOp",EDGE,"E90"),sQuery(id+"F0.wireOp",EDGE,"E91"),sQuery(id+"F0.wireOp",EDGE,"E92"),sQuery(id+"F0.wireOp",EDGE,"E93"),sQuery(id+"F0.wireOp",EDGE,"E94"),sQuery(id+"F0.wireOp",EDGE,"E95"),sQuery(id+"F0.wireOp",EDGE,"E96"),sQuery(id+"F0.wireOp",EDGE,"E97"),sQuery(id+"F0.wireOp",EDGE,"E98"),sQuery(id+"F0.wireOp",EDGE,"E99"),sQuery(id+"F0.wireOp",EDGE,"E100"),sQuery(id+"F0.wireOp",EDGE,"E101"),sQuery(id+"F0.wireOp",EDGE,"E102"),sQuery(id+"F0.wireOp",EDGE,"E103"),sQuery(id+"F0.wireOp",EDGE,"E104"),sQuery(id+"F0.wireOp",EDGE,"E105"),sQuery(id+"F0.wireOp",EDGE,"E106"),sQuery(id+"F0.wireOp",EDGE,"E107"),sQuery(id+"F0.wireOp",EDGE,"E108"),sQuery(id+"F0.wireOp",EDGE,"E109"),sQuery(id+"F0.wireOp",EDGE,"E110"),sQuery(id+"F0.wireOp",EDGE,"E111"),sQuery(id+"F0.wireOp",EDGE,"E112"),sQuery(id+"F0.wireOp",EDGE,"E113"),sQuery(id+"F0.wireOp",EDGE,"E114"),sQuery(id+"F0.wireOp",EDGE,"E115"),sQuery(id+"F0.wireOp",EDGE,"E116"),sQuery(id+"F0.wireOp",EDGE,"E117"),sQuery(id+"F0.wireOp",EDGE,"E118"),sQuery(id+"F0.wireOp",EDGE,"E119"),sQuery(id+"F0.wireOp",EDGE,"E120"),sQuery(id+"F0.wireOp",EDGE,"E121"),sQuery(id+"F0.wireOp",EDGE,"E122"),sQuery(id+"F0.wireOp",EDGE,"E123"),sQuery(id+"F0.wireOp",EDGE,"E124"),sQuery(id+"F0.wireOp",EDGE,"E125"),sQuery(id+"F0.wireOp",EDGE,"E126"),sQuery(id+"F0.wireOp",EDGE,"E127"),sQuery(id+"F0.wireOp",EDGE,"E128"),sQuery(id+"F0.wireOp",EDGE,"E129"),sQuery(id+"F0.wireOp",EDGE,"E130"),sQuery(id+"F0.wireOp",EDGE,"E131"),sQuery(id+"F0.wireOp",EDGE,"E132"),sQuery(id+"F0.wireOp",EDGE,"E133"),sQuery(id+"F0.wireOp",EDGE,"E134"),sQuery(id+"F0.wireOp",EDGE,"E135"),sQuery(id+"F0.wireOp",EDGE,"E136"),sQuery(id+"F0.wireOp",EDGE,"E137"),sQuery(id+"F0.wireOp",EDGE,"E138"),sQuery(id+"F0.wireOp",EDGE,"E139"),sQuery(id+"F0.wireOp",EDGE,"E140"),sQuery(id+"F0.wireOp",EDGE,"E141"),sQuery(id+"F0.wireOp",EDGE,"E142"),sQuery(id+"F0.wireOp",EDGE,"E143"),sQuery(id+"F0.wireOp",EDGE,"E144"),sQuery(id+"F0.wireOp",EDGE,"E145"),sQuery(id+"F0.wireOp",EDGE,"E146"),sQuery(id+"F0.wireOp",EDGE,"E147"),sQuery(id+"F0.wireOp",EDGE,"E148"),sQuery(id+"F0.wireOp",EDGE,"E149"),sQuery(id+"F0.wireOp",EDGE,"E150"),sQuery(id+"F0.wireOp",EDGE,"E151"),sQuery(id+"F0.wireOp",EDGE,"E152"),sQuery(id+"F0.wireOp",EDGE,"E153"),sQuery(id+"F0.wireOp",EDGE,"E154"),sQuery(id+"F0.wireOp",EDGE,"E155"),sQuery(id+"F0.wireOp",EDGE,"E156"),sQuery(id+"F0.wireOp",EDGE,"E157"),sQuery(id+"F0.wireOp",EDGE,"E158"),sQuery(id+"F0.wireOp",EDGE,"E159"),sQuery(id+"F0.wireOp",EDGE,"E160"),sQuery(id+"F0.wireOp",EDGE,"E161"),sQuery(id+"F0.wireOp",EDGE,"E162"),sQuery(id+"F0.wireOp",EDGE,"E163"),sQuery(id+"F0.wireOp",EDGE,"E164"),sQuery(id+"F0.wireOp",EDGE,"E165"),sQuery(id+"F0.wireOp",EDGE,"E166"),sQuery(id+"F0.wireOp",EDGE,"E167"),sQuery(id+"F0.wireOp",EDGE,"E168"),sQuery(id+"F0.wireOp",EDGE,"E169"),sQuery(id+"F0.wireOp",EDGE,"E170"),sQuery(id+"F0.wireOp",EDGE,"E171"),sQuery(id+"F0.wireOp",EDGE,"E172"),sQuery(id+"F0.wireOp",EDGE,"E173"),sQuery(id+"F0.wireOp",EDGE,"E174"),sQuery(id+"F0.wireOp",EDGE,"E175"),sQuery(id+"F0.wireOp",EDGE,"E176"),sQuery(id+"F0.wireOp",EDGE,"E177"),sQuery(id+"F0.wireOp",EDGE,"E178"),sQuery(id+"F0.wireOp",EDGE,"E179"),sQuery(id+"F0.wireOp",EDGE,"E180"),sQuery(id+"F0.wireOp",EDGE,"E181"),sQuery(id+"F0.wireOp",EDGE,"E182"),sQuery(id+"F0.wireOp",EDGE,"E183"),sQuery(id+"F0.wireOp",EDGE,"E184"),sQuery(id+"F0.wireOp",EDGE,"E185"),sQuery(id+"F0.wireOp",EDGE,"E186"),sQuery(id+"F0.wireOp",EDGE,"E187"),sQuery(id+"F0.wireOp",EDGE,"E188"),sQuery(id+"F0.wireOp",EDGE,"E189"),sQuery(id+"F0.wireOp",EDGE,"E190"),sQuery(id+"F0.wireOp",EDGE,"E191"),sQuery(id+"F0.wireOp",EDGE,"E192"),sQuery(id+"F0.wireOp",EDGE,"E193"),sQuery(id+"F0.wireOp",EDGE,"E194"),sQuery(id+"F0.wireOp",EDGE,"E195"),sQuery(id+"F0.wireOp",EDGE,"E196"),sQuery(id+"F0.wireOp",EDGE,"E197"),sQuery(id+"F0.wireOp",EDGE,"E198"),sQuery(id+"F0.wireOp",EDGE,"E199"),sQuery(id+"F0.wireOp",EDGE,"E200"),sQuery(id+"F0.wireOp",EDGE,"E201"),sQuery(id+"F0.wireOp",EDGE,"E202"),sQuery(id+"F0.wireOp",EDGE,"E203"),sQuery(id+"F0.wireOp",EDGE,"E204"),sQuery(id+"F0.wireOp",EDGE,"E205"),sQuery(id+"F0.wireOp",EDGE,"E206"),sQuery(id+"F0.wireOp",EDGE,"E207"),sQuery(id+"F0.wireOp",EDGE,"E208"),sQuery(id+"F0.wireOp",EDGE,"E209"),sQuery(id+"F0.wireOp",EDGE,"E210"),sQuery(id+"F0.wireOp",EDGE,"E211"),sQuery(id+"F0.wireOp",EDGE,"E212"),sQuery(id+"F0.wireOp",EDGE,"E213"),sQuery(id+"F0.wireOp",EDGE,"E214"),sQuery(id+"F0.wireOp",EDGE,"E215"),sQuery(id+"F0.wireOp",EDGE,"E216"),sQuery(id+"F0.wireOp",EDGE,"E217"),sQuery(id+"F0.wireOp",EDGE,"E218"),sQuery(id+"F0.wireOp",EDGE,"E219"),sQuery(id+"F0.wireOp",EDGE,"E220"),sQuery(id+"F0.wireOp",EDGE,"E221"),sQuery(id+"F0.wireOp",EDGE,"E222"),sQuery(id+"F0.wireOp",EDGE,"E223"),sQuery(id+"F0.wireOp",EDGE,"E224"),sQuery(id+"F0.wireOp",EDGE,"E225"),sQuery(id+"F0.wireOp",EDGE,"E226"),sQuery(id+"F0.wireOp",EDGE,"E227"),sQuery(id+"F0.wireOp",EDGE,"E228"),sQuery(id+"F0.wireOp",EDGE,"E229"),sQuery(id+"F0.wireOp",EDGE,"E230"),sQuery(id+"F0.wireOp",EDGE,"E231"),sQuery(id+"F0.wireOp",EDGE,"E232"),sQuery(id+"F0.wireOp",EDGE,"E233"),sQuery(id+"F0.wireOp",EDGE,"E234"),sQuery(id+"F0.wireOp",EDGE,"E235"),sQuery(id+"F0.wireOp",EDGE,"E236"),sQuery(id+"F0.wireOp",EDGE,"E237"),sQuery(id+"F0.wireOp",EDGE,"E238"),sQuery(id+"F0.wireOp",EDGE,"E239"),sQuery(id+"F0.wireOp",EDGE,"E240"),sQuery(id+"F0.wireOp",EDGE,"E241"),sQuery(id+"F0.wireOp",EDGE,"E242"),sQuery(id+"F0.wireOp",EDGE,"E243"),sQuery(id+"F0.wireOp",EDGE,"E244"),sQuery(id+"F0.wireOp",EDGE,"E245"),sQuery(id+"F0.wireOp",EDGE,"E246"),sQuery(id+"F0.wireOp",EDGE,"E247"),sQuery(id+"F0.wireOp",EDGE,"E248"),sQuery(id+"F0.wireOp",EDGE,"E249"),sQuery(id+"F0.wireOp",EDGE,"E250"),sQuery(id+"F0.wireOp",EDGE,"E251"),sQuery(id+"F0.wireOp",EDGE,"E252"),sQuery(id+"F0.wireOp",EDGE,"E253"),sQuery(id+"F0.wireOp",EDGE,"E254"),sQuery(id+"F0.wireOp",EDGE,"E255"),sQuery(id+"F0.wireOp",EDGE,"E256"),sQuery(id+"F0.wireOp",EDGE,"E257"),sQuery(id+"F0.wireOp",EDGE,"E258"),sQuery(id+"F0.wireOp",EDGE,"E259"),sQuery(id+"F0.wireOp",EDGE,"E260"),sQuery(id+"F0.wireOp",EDGE,"E261")])]});
            transform(context, id + "F5", {"entities" : qUnion([Q0]), "transformType" : TransformType.TRANSLATION_3D, "dx" : 0 * mm, "dy" : -172 * mm, "dz" : 0 * mm, "makeCopy" : true});
        }
        {
            var Q0;
            Q0=makeQuery(id+"F5.opPattern","COPY",FACE,{"derivedFrom":makeQuery(id+"F1.opExtrude","CAP_FACE",FACE,{"disambiguationData":[OSD([sQuery(id+"F0.wireOp",EDGE,"E0"),sQuery(id+"F0.wireOp",EDGE,"E1"),sQuery(id+"F0.wireOp",EDGE,"E2"),sQuery(id+"F0.wireOp",EDGE,"E3"),sQuery(id+"F0.wireOp",EDGE,"E4"),sQuery(id+"F0.wireOp",EDGE,"E5"),sQuery(id+"F0.wireOp",EDGE,"E6"),sQuery(id+"F0.wireOp",EDGE,"E7"),sQuery(id+"F0.wireOp",EDGE,"E8"),sQuery(id+"F0.wireOp",EDGE,"E9"),sQuery(id+"F0.wireOp",EDGE,"E10"),sQuery(id+"F0.wireOp",EDGE,"E11"),sQuery(id+"F0.wireOp",EDGE,"E12"),sQuery(id+"F0.wireOp",EDGE,"E13"),sQuery(id+"F0.wireOp",EDGE,"E14"),sQuery(id+"F0.wireOp",EDGE,"E15"),sQuery(id+"F0.wireOp",EDGE,"E16"),sQuery(id+"F0.wireOp",EDGE,"E17"),sQuery(id+"F0.wireOp",EDGE,"E18"),sQuery(id+"F0.wireOp",EDGE,"E19"),sQuery(id+"F0.wireOp",EDGE,"E20"),sQuery(id+"F0.wireOp",EDGE,"E21"),sQuery(id+"F0.wireOp",EDGE,"E22"),sQuery(id+"F0.wireOp",EDGE,"E23"),sQuery(id+"F0.wireOp",EDGE,"E24"),sQuery(id+"F0.wireOp",EDGE,"E25"),sQuery(id+"F0.wireOp",EDGE,"E26"),sQuery(id+"F0.wireOp",EDGE,"E27"),sQuery(id+"F0.wireOp",EDGE,"E28"),sQuery(id+"F0.wireOp",EDGE,"E29"),sQuery(id+"F0.wireOp",EDGE,"E30"),sQuery(id+"F0.wireOp",EDGE,"E31"),sQuery(id+"F0.wireOp",EDGE,"E32"),sQuery(id+"F0.wireOp",EDGE,"E33"),sQuery(id+"F0.wireOp",EDGE,"E34"),sQuery(id+"F0.wireOp",EDGE,"E35"),sQuery(id+"F0.wireOp",EDGE,"E36"),sQuery(id+"F0.wireOp",EDGE,"E37"),sQuery(id+"F0.wireOp",EDGE,"E38"),sQuery(id+"F0.wireOp",EDGE,"E39"),sQuery(id+"F0.wireOp",EDGE,"E40"),sQuery(id+"F0.wireOp",EDGE,"E41"),sQuery(id+"F0.wireOp",EDGE,"E42"),sQuery(id+"F0.wireOp",EDGE,"E43"),sQuery(id+"F0.wireOp",EDGE,"E44"),sQuery(id+"F0.wireOp",EDGE,"E45"),sQuery(id+"F0.wireOp",EDGE,"E46"),sQuery(id+"F0.wireOp",EDGE,"E47"),sQuery(id+"F0.wireOp",EDGE,"E48"),sQuery(id+"F0.wireOp",EDGE,"E49"),sQuery(id+"F0.wireOp",EDGE,"E50"),sQuery(id+"F0.wireOp",EDGE,"E51"),sQuery(id+"F0.wireOp",EDGE,"E52"),sQuery(id+"F0.wireOp",EDGE,"E53"),sQuery(id+"F0.wireOp",EDGE,"E54"),sQuery(id+"F0.wireOp",EDGE,"E55"),sQuery(id+"F0.wireOp",EDGE,"E56"),sQuery(id+"F0.wireOp",EDGE,"E57"),sQuery(id+"F0.wireOp",EDGE,"E58"),sQuery(id+"F0.wireOp",EDGE,"E59"),sQuery(id+"F0.wireOp",EDGE,"E60"),sQuery(id+"F0.wireOp",EDGE,"E61"),sQuery(id+"F0.wireOp",EDGE,"E62"),sQuery(id+"F0.wireOp",EDGE,"E63"),sQuery(id+"F0.wireOp",EDGE,"E64"),sQuery(id+"F0.wireOp",EDGE,"E65"),sQuery(id+"F0.wireOp",EDGE,"E66"),sQuery(id+"F0.wireOp",EDGE,"E67"),sQuery(id+"F0.wireOp",EDGE,"E68"),sQuery(id+"F0.wireOp",EDGE,"E69"),sQuery(id+"F0.wireOp",EDGE,"E70"),sQuery(id+"F0.wireOp",EDGE,"E71"),sQuery(id+"F0.wireOp",EDGE,"E72"),sQuery(id+"F0.wireOp",EDGE,"E73"),sQuery(id+"F0.wireOp",EDGE,"E74"),sQuery(id+"F0.wireOp",EDGE,"E75"),sQuery(id+"F0.wireOp",EDGE,"E76"),sQuery(id+"F0.wireOp",EDGE,"E77"),sQuery(id+"F0.wireOp",EDGE,"E78"),sQuery(id+"F0.wireOp",EDGE,"E79"),sQuery(id+"F0.wireOp",EDGE,"E80"),sQuery(id+"F0.wireOp",EDGE,"E81"),sQuery(id+"F0.wireOp",EDGE,"E82"),sQuery(id+"F0.wireOp",EDGE,"E83"),sQuery(id+"F0.wireOp",EDGE,"E84"),sQuery(id+"F0.wireOp",EDGE,"E85"),sQuery(id+"F0.wireOp",EDGE,"E86"),sQuery(id+"F0.wireOp",EDGE,"E87"),sQuery(id+"F0.wireOp",EDGE,"E88"),sQuery(id+"F0.wireOp",EDGE,"E89"),sQuery(id+"F0.wireOp",EDGE,"E90"),sQuery(id+"F0.wireOp",EDGE,"E91"),sQuery(id+"F0.wireOp",EDGE,"E92"),sQuery(id+"F0.wireOp",EDGE,"E93"),sQuery(id+"F0.wireOp",EDGE,"E94"),sQuery(id+"F0.wireOp",EDGE,"E95"),sQuery(id+"F0.wireOp",EDGE,"E96"),sQuery(id+"F0.wireOp",EDGE,"E97"),sQuery(id+"F0.wireOp",EDGE,"E98"),sQuery(id+"F0.wireOp",EDGE,"E99"),sQuery(id+"F0.wireOp",EDGE,"E100"),sQuery(id+"F0.wireOp",EDGE,"E101"),sQuery(id+"F0.wireOp",EDGE,"E102"),sQuery(id+"F0.wireOp",EDGE,"E103"),sQuery(id+"F0.wireOp",EDGE,"E104"),sQuery(id+"F0.wireOp",EDGE,"E105"),sQuery(id+"F0.wireOp",EDGE,"E106"),sQuery(id+"F0.wireOp",EDGE,"E107"),sQuery(id+"F0.wireOp",EDGE,"E108"),sQuery(id+"F0.wireOp",EDGE,"E109"),sQuery(id+"F0.wireOp",EDGE,"E110"),sQuery(id+"F0.wireOp",EDGE,"E111"),sQuery(id+"F0.wireOp",EDGE,"E112"),sQuery(id+"F0.wireOp",EDGE,"E113"),sQuery(id+"F0.wireOp",EDGE,"E114"),sQuery(id+"F0.wireOp",EDGE,"E115"),sQuery(id+"F0.wireOp",EDGE,"E116"),sQuery(id+"F0.wireOp",EDGE,"E117"),sQuery(id+"F0.wireOp",EDGE,"E118"),sQuery(id+"F0.wireOp",EDGE,"E119"),sQuery(id+"F0.wireOp",EDGE,"E120"),sQuery(id+"F0.wireOp",EDGE,"E121"),sQuery(id+"F0.wireOp",EDGE,"E122"),sQuery(id+"F0.wireOp",EDGE,"E123"),sQuery(id+"F0.wireOp",EDGE,"E124"),sQuery(id+"F0.wireOp",EDGE,"E125"),sQuery(id+"F0.wireOp",EDGE,"E126"),sQuery(id+"F0.wireOp",EDGE,"E127"),sQuery(id+"F0.wireOp",EDGE,"E128"),sQuery(id+"F0.wireOp",EDGE,"E129"),sQuery(id+"F0.wireOp",EDGE,"E130"),sQuery(id+"F0.wireOp",EDGE,"E131"),sQuery(id+"F0.wireOp",EDGE,"E132"),sQuery(id+"F0.wireOp",EDGE,"E133"),sQuery(id+"F0.wireOp",EDGE,"E134"),sQuery(id+"F0.wireOp",EDGE,"E135"),sQuery(id+"F0.wireOp",EDGE,"E136"),sQuery(id+"F0.wireOp",EDGE,"E137"),sQuery(id+"F0.wireOp",EDGE,"E138"),sQuery(id+"F0.wireOp",EDGE,"E139"),sQuery(id+"F0.wireOp",EDGE,"E140"),sQuery(id+"F0.wireOp",EDGE,"E141"),sQuery(id+"F0.wireOp",EDGE,"E142"),sQuery(id+"F0.wireOp",EDGE,"E143"),sQuery(id+"F0.wireOp",EDGE,"E144"),sQuery(id+"F0.wireOp",EDGE,"E145"),sQuery(id+"F0.wireOp",EDGE,"E146"),sQuery(id+"F0.wireOp",EDGE,"E147"),sQuery(id+"F0.wireOp",EDGE,"E148"),sQuery(id+"F0.wireOp",EDGE,"E149"),sQuery(id+"F0.wireOp",EDGE,"E150"),sQuery(id+"F0.wireOp",EDGE,"E151"),sQuery(id+"F0.wireOp",EDGE,"E152"),sQuery(id+"F0.wireOp",EDGE,"E153"),sQuery(id+"F0.wireOp",EDGE,"E154"),sQuery(id+"F0.wireOp",EDGE,"E155"),sQuery(id+"F0.wireOp",EDGE,"E156"),sQuery(id+"F0.wireOp",EDGE,"E157"),sQuery(id+"F0.wireOp",EDGE,"E158"),sQuery(id+"F0.wireOp",EDGE,"E159"),sQuery(id+"F0.wireOp",EDGE,"E160"),sQuery(id+"F0.wireOp",EDGE,"E161"),sQuery(id+"F0.wireOp",EDGE,"E162"),sQuery(id+"F0.wireOp",EDGE,"E163"),sQuery(id+"F0.wireOp",EDGE,"E164"),sQuery(id+"F0.wireOp",EDGE,"E165"),sQuery(id+"F0.wireOp",EDGE,"E166"),sQuery(id+"F0.wireOp",EDGE,"E167"),sQuery(id+"F0.wireOp",EDGE,"E168"),sQuery(id+"F0.wireOp",EDGE,"E169"),sQuery(id+"F0.wireOp",EDGE,"E170"),sQuery(id+"F0.wireOp",EDGE,"E171"),sQuery(id+"F0.wireOp",EDGE,"E172"),sQuery(id+"F0.wireOp",EDGE,"E173"),sQuery(id+"F0.wireOp",EDGE,"E174"),sQuery(id+"F0.wireOp",EDGE,"E175"),sQuery(id+"F0.wireOp",EDGE,"E176"),sQuery(id+"F0.wireOp",EDGE,"E177"),sQuery(id+"F0.wireOp",EDGE,"E178"),sQuery(id+"F0.wireOp",EDGE,"E179"),sQuery(id+"F0.wireOp",EDGE,"E180"),sQuery(id+"F0.wireOp",EDGE,"E181"),sQuery(id+"F0.wireOp",EDGE,"E182"),sQuery(id+"F0.wireOp",EDGE,"E183"),sQuery(id+"F0.wireOp",EDGE,"E184"),sQuery(id+"F0.wireOp",EDGE,"E185"),sQuery(id+"F0.wireOp",EDGE,"E186"),sQuery(id+"F0.wireOp",EDGE,"E187"),sQuery(id+"F0.wireOp",EDGE,"E188"),sQuery(id+"F0.wireOp",EDGE,"E189"),sQuery(id+"F0.wireOp",EDGE,"E190"),sQuery(id+"F0.wireOp",EDGE,"E191"),sQuery(id+"F0.wireOp",EDGE,"E192"),sQuery(id+"F0.wireOp",EDGE,"E193"),sQuery(id+"F0.wireOp",EDGE,"E194"),sQuery(id+"F0.wireOp",EDGE,"E195"),sQuery(id+"F0.wireOp",EDGE,"E196"),sQuery(id+"F0.wireOp",EDGE,"E197"),sQuery(id+"F0.wireOp",EDGE,"E198"),sQuery(id+"F0.wireOp",EDGE,"E199"),sQuery(id+"F0.wireOp",EDGE,"E200"),sQuery(id+"F0.wireOp",EDGE,"E201"),sQuery(id+"F0.wireOp",EDGE,"E202"),sQuery(id+"F0.wireOp",EDGE,"E203"),sQuery(id+"F0.wireOp",EDGE,"E204"),sQuery(id+"F0.wireOp",EDGE,"E205"),sQuery(id+"F0.wireOp",EDGE,"E206"),sQuery(id+"F0.wireOp",EDGE,"E207"),sQuery(id+"F0.wireOp",EDGE,"E208"),sQuery(id+"F0.wireOp",EDGE,"E209"),sQuery(id+"F0.wireOp",EDGE,"E210"),sQuery(id+"F0.wireOp",EDGE,"E211"),sQuery(id+"F0.wireOp",EDGE,"E212"),sQuery(id+"F0.wireOp",EDGE,"E213"),sQuery(id+"F0.wireOp",EDGE,"E214"),sQuery(id+"F0.wireOp",EDGE,"E215"),sQuery(id+"F0.wireOp",EDGE,"E216"),sQuery(id+"F0.wireOp",EDGE,"E217"),sQuery(id+"F0.wireOp",EDGE,"E218"),sQuery(id+"F0.wireOp",EDGE,"E219"),sQuery(id+"F0.wireOp",EDGE,"E220"),sQuery(id+"F0.wireOp",EDGE,"E221"),sQuery(id+"F0.wireOp",EDGE,"E222"),sQuery(id+"F0.wireOp",EDGE,"E223"),sQuery(id+"F0.wireOp",EDGE,"E224"),sQuery(id+"F0.wireOp",EDGE,"E225"),sQuery(id+"F0.wireOp",EDGE,"E226"),sQuery(id+"F0.wireOp",EDGE,"E227"),sQuery(id+"F0.wireOp",EDGE,"E228"),sQuery(id+"F0.wireOp",EDGE,"E229"),sQuery(id+"F0.wireOp",EDGE,"E230"),sQuery(id+"F0.wireOp",EDGE,"E231"),sQuery(id+"F0.wireOp",EDGE,"E232"),sQuery(id+"F0.wireOp",EDGE,"E233"),sQuery(id+"F0.wireOp",EDGE,"E234"),sQuery(id+"F0.wireOp",EDGE,"E235"),sQuery(id+"F0.wireOp",EDGE,"E236"),sQuery(id+"F0.wireOp",EDGE,"E237"),sQuery(id+"F0.wireOp",EDGE,"E238"),sQuery(id+"F0.wireOp",EDGE,"E239"),sQuery(id+"F0.wireOp",EDGE,"E240"),sQuery(id+"F0.wireOp",EDGE,"E241"),sQuery(id+"F0.wireOp",EDGE,"E242"),sQuery(id+"F0.wireOp",EDGE,"E243"),sQuery(id+"F0.wireOp",EDGE,"E244"),sQuery(id+"F0.wireOp",EDGE,"E245"),sQuery(id+"F0.wireOp",EDGE,"E246"),sQuery(id+"F0.wireOp",EDGE,"E247"),sQuery(id+"F0.wireOp",EDGE,"E248"),sQuery(id+"F0.wireOp",EDGE,"E249"),sQuery(id+"F0.wireOp",EDGE,"E250"),sQuery(id+"F0.wireOp",EDGE,"E251"),sQuery(id+"F0.wireOp",EDGE,"E252"),sQuery(id+"F0.wireOp",EDGE,"E253"),sQuery(id+"F0.wireOp",EDGE,"E254"),sQuery(id+"F0.wireOp",EDGE,"E255"),sQuery(id+"F0.wireOp",EDGE,"E256"),sQuery(id+"F0.wireOp",EDGE,"E257"),sQuery(id+"F0.wireOp",EDGE,"E258"),sQuery(id+"F0.wireOp",EDGE,"E259"),sQuery(id+"F0.wireOp",EDGE,"E260"),sQuery(id+"F0.wireOp",EDGE,"E261")])],"isStart":false}),"instanceName":"1"});
            var sketch = newSketch(context, id + "F6", { "sketchPlane" : qUnion([Q0])});
            skLineSegment(sketch, "E275.bottom", {"start": v(-28.07, -132.15) * mm, "end": v(28.07, -132.15) * mm});
            skLineSegment(sketch, "E275.top", {"start": v(-28.07, -194.15) * mm, "end": v(28.07, -194.15) * mm});
            skLineSegment(sketch, "E275.left", {"start": v(-28.07, -132.15) * mm, "end": v(-28.07, -194.15) * mm});
            skLineSegment(sketch, "E275.right", {"start": v(28.07, -132.15) * mm, "end": v(28.07, -194.15) * mm});
            skSolve(sketch);
        }
        {
            var Q0;
            Q0=makeQuery(id+"F6.imprint","IMPRINT",FACE,{"disambiguationData":[TD([[makeQuery(id+"F6.imprint","IMPRINT",EDGE,{"derivedFrom":makeQuery(id+"F5.opPattern","COPY",EDGE,{"derivedFrom":makeQuery(id+"F1.opExtrude","CAP_EDGE",EDGE,{"disambiguationData":[OSD([sQuery(id+"F0.wireOp",EDGE,"E1")])],"isStart":false}),"instanceName":"1"})}),1.0]])]});
            extrude(context, id + "F7", {"entities" : qUnion([Q0]), "operationType" : NewBodyOperationType.REMOVE, "oppositeDirection" : true, "depth" : 25 * mm, "offsetDistance" : 25 * mm});
        }
        {
            var Q0;
            Q0=makeQuery(id+"F1.opExtrude","CAP_EDGE",EDGE,{"disambiguationData":[OSD([sQuery(id+"F0.wireOp",EDGE,"E150")])],"isStart":true});
            cPoint(context, id + "F8", {"entities" : qUnion([Q0]), "parameter" : 0.5});
        }
        {
            var Q0;
            Q0 = qCreatedBy(id + "F8" ,VERTEX);
            var Q1;
            Q1=makeQuery(id+"F1.opExtrude","CAP_EDGE",EDGE,{"disambiguationData":[OSD([sQuery(id+"F0.wireOp",EDGE,"E150")])],"isStart":true});
            cPlane(context, id + "F9", {"entities" : qUnion([Q0, Q1]), "cplaneType" : CPlaneType.LINE_POINT, "offset" : 25 * mm, "width" : 150 * mm, "height" : 150 * mm});
        }
        {
            var Q0;
            Q0=qCreatedBy(id+"F9.planeOp",FACE);
            var sketch = newSketch(context, id + "F10", { "sketchPlane" : qUnion([Q0])});
            skCircle(sketch, "E276", {"center": v(-85, -6) * mm, "radius": 7.5 * mm, "construction": true});
            skCircle(sketch, "E277", {"center": v(85, -6) * mm, "radius": 7.5 * mm, "construction": true});
            skSolve(sketch);
        }
        {
            var Q0;
            Q0=makeQuery(id+"F1.opExtrude","CAP_EDGE",EDGE,{"disambiguationData":[OSD([sQuery(id+"F0.wireOp",EDGE,"E134")])],"isStart":true});
            cPoint(context, id + "F11", {"entities" : qUnion([Q0]), "parameter" : 0.5});
        }
        {
            var Q0;
            Q0 = qCreatedBy(id + "F11" ,VERTEX);
            var Q1;
            Q1=makeQuery(id+"F1.opExtrude","CAP_EDGE",EDGE,{"disambiguationData":[OSD([sQuery(id+"F0.wireOp",EDGE,"E134")])],"isStart":true});
            cPlane(context, id + "F12", {"entities" : qUnion([Q0, Q1]), "cplaneType" : CPlaneType.LINE_POINT, "offset" : 25 * mm, "width" : 150 * mm, "height" : 150 * mm});
        }
        {
            var Q0;
            Q0=qCreatedBy(id+"F12.planeOp",FACE);
            var sketch = newSketch(context, id + "F13", { "sketchPlane" : qUnion([Q0])});
            skCircle(sketch, "E278", {"center": v(-85, -6) * mm, "radius": 7.5 * mm, "construction": true});
            skCircle(sketch, "E279", {"center": v(85, -6) * mm, "radius": 7.5 * mm, "construction": true});
            skSolve(sketch);
        }
    });
